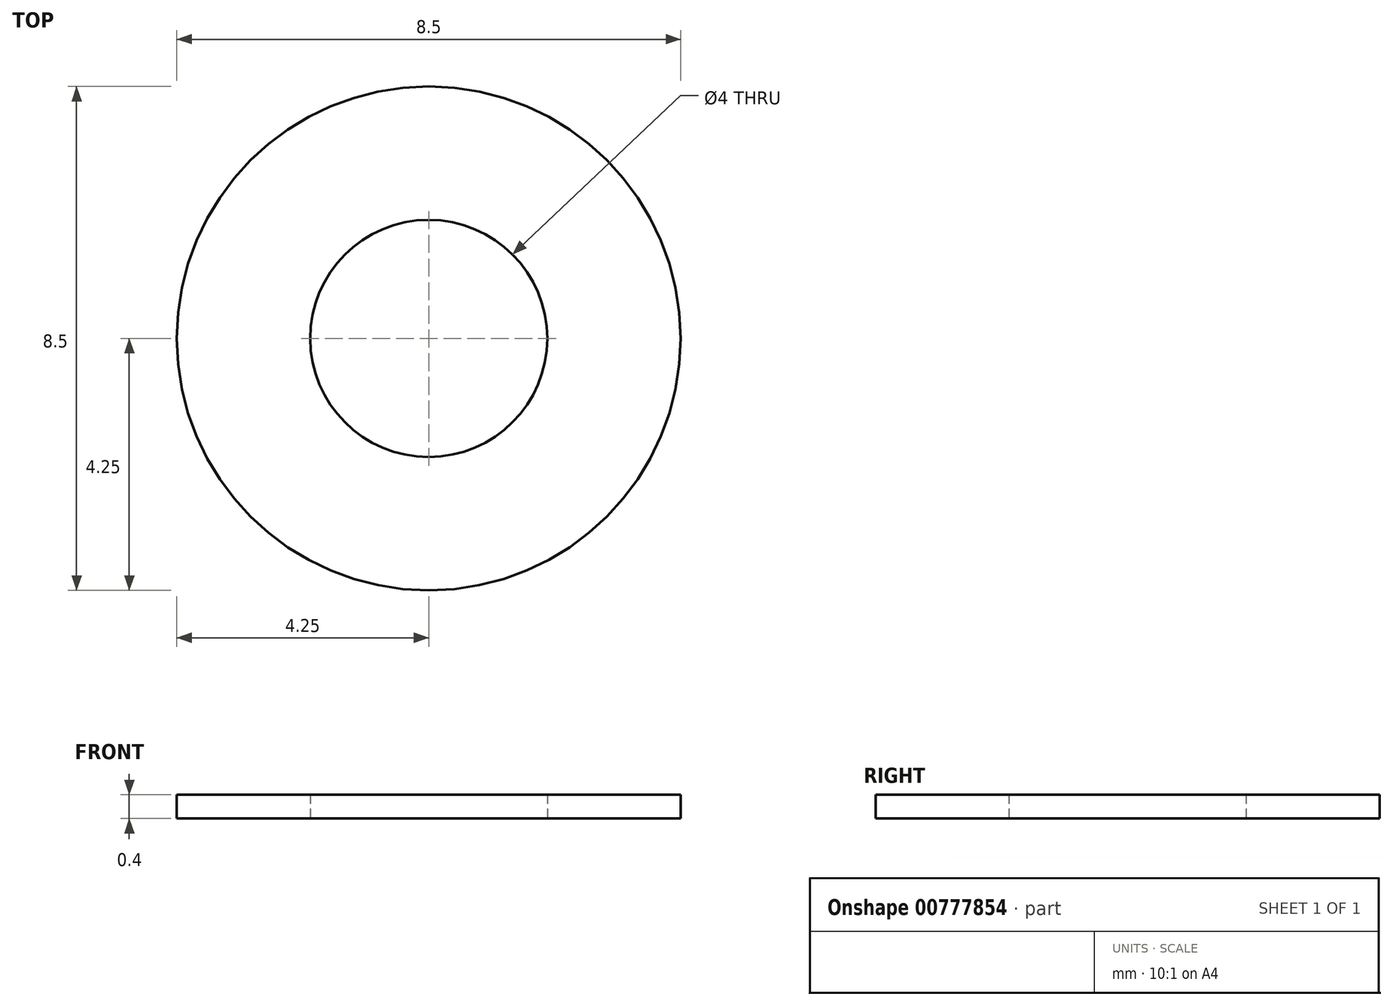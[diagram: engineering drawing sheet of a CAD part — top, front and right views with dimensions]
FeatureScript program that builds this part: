
annotation { "Feature Type Name" : "Feature", "Feature Type Description" : "" }
export const myFeature = defineFeature(function(context is Context, id is Id, definition is map)
    precondition{}
    {
        {
            var Q0;
            Q0=qCreatedBy(makeId("Top.planeOp"),FACE);
            var sketch = newSketch(context, id + "F0", { "sketchPlane" : qUnion([Q0])});
            skCircle(sketch, "E0", {"center": v(0, 0) * mm, "radius": 2 * mm});
            skCircle(sketch, "E1", {"center": v(0, 0) * mm, "radius": 4.25 * mm});
            skSolve(sketch);
        }
        {
            var Q0;
            Q0 = qSketchRegion(id + "F0", true);
            extrude(context, id + "F1", {"entities" : qUnion([Q0]), "depth" : .4 * mm, "offsetDistance" : 25 * mm});
        }
    });
